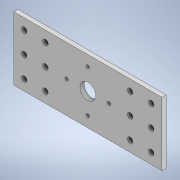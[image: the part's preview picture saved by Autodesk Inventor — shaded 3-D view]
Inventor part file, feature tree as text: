
AUTODESK INVENTOR PART (.ipt)
format: ipt  version: 2020 (Build 240168000, 168)  size: 158,720 bytes
history: native  units: in
note: dims shown in document units (in); Inventor stores cm internally (conversion verified against a paired STEP export)
features: extrude x1, sketch x1
ambient origin geometry x8: Origin, YZ Plane, XZ Plane, XY Plane, X Axis, Y Axis, Z Axis, Center Point
bodies: Body1 (feature_tree)
feature tree (2):
  extrude  "Extrusion3"  Depth=3.0in
  sketch  "Sketch1"  dims[d0=7.0in d1=3.0in d2=0.75in d3=1.5in d4=3.5in d5=0.159in d6=1.0in d7=3.5in d8=0.159in d9=1.0in d10=1.5in d11=0.7874in d13=2.0in d14=0.3937in d16=1.0in d18=0.7874in d20=2.0in d21=0.3937in d23=1.0in d25=0.256in d26=0.5in d27=0.5in d28=1.1811in d30=1.0in d31=0.3937in d33=1.0in d37=0.7874in d39=1.0in d40=0.3937in d42=1.0in d46=0.7874in d48=5.0in d49=0.3937in d51=1.0in d53=0.7874in d55=1.0in d56=0.3937in d58=1.0in d60=0.2in d61=0.0in]
